# Revit family: fate vsb- hole
name_source: partatom
category: Plumbing Fixtures
units: mm (PartAtom-declared; Revit-internal decimal feet)

## family parameters
Always vertical = No
Cut with Voids When Loaded = Yes
OmniClass Number = 23.45.05.14.14
OmniClass Title = Sinks/Lavatories
Part Type = Normal
Room Calculation Point = No
Round Connector Dimension = Use Diameter
Shared = Yes
Work Plane-Based = Yes

## types (2) — shared parameters
Assembly Code = D2010310
Basin Shape = Square
Bowl Depth = 3 3/4"
Bowl Length = 15 3/8"
Bowl Width = 19"
CW Connection = Yes
CWFU = 1.5
Cold Water Connection Diameter = 1/2"
Cold Water Connection Width = 3"
Compliance Certifications = Meets or Exceeds CSA B45.5 / IAPMO Z124
Default Elevation = 34"
Finish = Acrylic-DXV-415-Canvas White-Glossy
Grid Drain = No
HW Connection = Yes
HWFU = 1.5
Height = 5 1/16"
Hot Water Connection Diameter = 1/2"
Hot Water Connection Width = 3"
Installation Instruction Link = https://dxv01.blob.core.windows.net
Installation Type = Topmount
Length = 21"
Manufacturer = DXV
Material = Acrylic-DXV-415-Canvas White-Glossy
Optional D29005000.415 Drain Plate = No
Price = Prices may vary. Please consult Manufacturer Rep for most up-to-date price list.
Product Documentation Link = https://dxv01.blob.core.windows.net
Product Page URL = https://www.dxv.com
Revised Date = 04/18/2022
URL = https://www.dxv.com
Vent Connection = No
WFU = 2
Waste Connection = Yes
Waste Connection Diameter = 1 1/4"
Width = 21"

## per-type parameters (varying)
| type | Description | Single-Hole |
| D21040021.415 | DXV Modulus 21-inch Bathroom Sink | 6" |
| D21040021001.415 | DXV Modulus 21-inch Single-Hole Bathroom Sink | 2 3/8" |

note: column(s) folded — value = type name in every type: Model

type visibility flags (boolean, named after types; folded from table):
- D21040021.415: Yes: D21040021.415  No-Hole Lavatory
- D21040021001.415: Yes: D21040021001.415 Single-Hole Lavatory

## geometry (parser evidence)
native form markers: Sweep x2
no freeform markers — native parametric forms only
